# Revit family: 32_Berkvens_Avento RZ 60PLUS brandwerend + Berkopal stomp
name_source: partatom
category: Doors
units: mm (PartAtom-declared; Revit-internal decimal feet)

## family parameters
Always vertical = Yes
Cut with Voids When Loaded = No
Host = Wall
OmniClass Number = 23.30.10.00
OmniClass Title = Doors
Room Calculation Point = No
Shared = No

## types (3) — shared parameters
60_45 Model kozijn = RZ enkeldeurs
60_81 Uitvoering kozijn = 60 plus brandwerend kozijn zonder bovenlicht
60_84 Type kozijn = Avento stalen montagekozijn 1,5 mm
70_88 Uitvoering deur = standaard
70_90 Type deur = Berkopal, HPLdeur
80_30 Krukgathoogte = 1050 mm
80_60 Kantuitvoering = stomp
80_75 Deurhoogte = 2315 mm  [stored 7.59514 ft]
Analytic Construction = <None>
Function = Interior
M1 = Berkvens <maak keuze>
M2 = Berkvens_kristalwit
M3 = Berkvens_reinwit
M4 = Berkvens_reinwit
M5 = Berkvens_kristalwit
M6 = Berkvens_gebroken wit
Manufacturer = Berkvens
Model = Avento RZ
URL = www.berkvens.nl
Versie = 1.0
Wall Closure = By host
zero-valued in all types: Height, Width

## per-type parameters (varying)
| type | 60_51 Sparingsmaat | 60_63 Vloerplafondhoogte | 80_90 Deurbreedte actieve deur | Assembly Code | Compartmentation | FireExit | IsExternal | SelfClosing | SmokeStop | dbn |
| 930X2315 | 976 mm | 0 mm  [stored 0 ft] | 930 mm  [stored 3.05118 ft] | 32.31 | No | No | No | No | No | 926 mm  [stored 3.03806 ft] |
| 880x2315 | 926 mm  [stored 3.03806 ft] | 2650 mm | 880 mm |  | Yes | Yes | Yes | Yes | Yes | 876 mm |
| 730x2315 | 926 mm  [stored 3.03806 ft] | 2650 mm | 880 mm |  | Yes | Yes | Yes | Yes | Yes | 876 mm |

note: [stored X ft] marks values corroborated as IEEE doubles in the binary element streams (Revit-internal decimal feet)

## geometry (parser evidence)
native form markers: Sweep x37
no freeform markers — native parametric forms only
